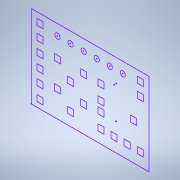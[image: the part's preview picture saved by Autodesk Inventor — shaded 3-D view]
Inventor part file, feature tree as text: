
AUTODESK INVENTOR PART (.ipt)
format: ipt  version: 2021.1 (Build 251245000, 245)  size: 135,680 bytes
history: native  units: mm
features: sketch x1
ambient origin geometry x8: Origin, YZ Plane, XZ Plane, XY Plane, X Axis, Y Axis, Z Axis, Center Point
feature tree (1):
  sketch  "Sketch2"
